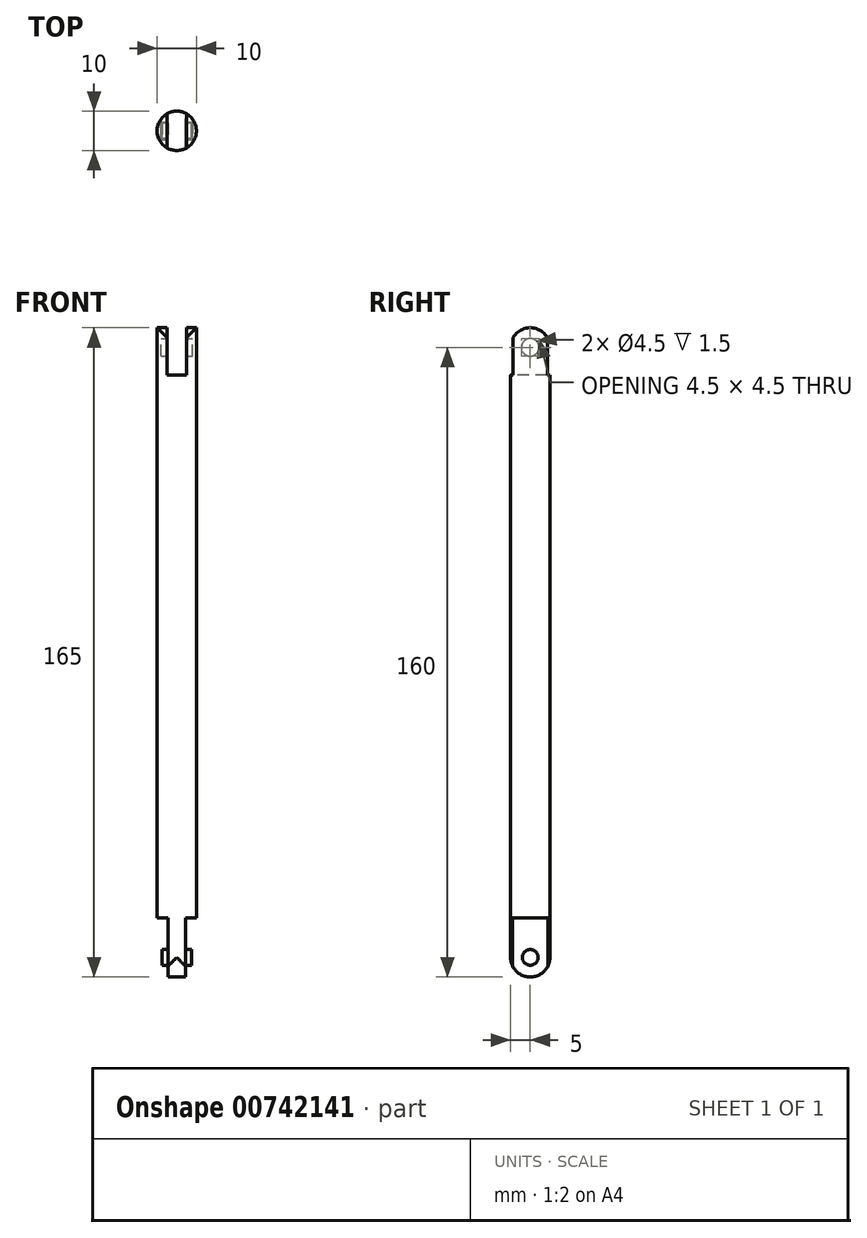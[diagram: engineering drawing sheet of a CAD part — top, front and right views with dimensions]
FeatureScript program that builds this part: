
annotation { "Feature Type Name" : "Feature", "Feature Type Description" : "" }
export const myFeature = defineFeature(function(context is Context, id is Id, definition is map)
    precondition{}
    {
        {
            var Q0;
            Q0=qCreatedBy(makeId("Top.planeOp"),FACE);
            var sketch = newSketch(context, id + "F0", { "sketchPlane" : qUnion([Q0])});
            skCircle(sketch, "E0", {"center": v(0, 0) * mm, "radius": 5 * mm});
            skSolve(sketch);
        }
        {
            var Q0;
            Q0=qSketchRegion(id+"F0",true);
            extrude(context, id + "F1", {"entities" : qUnion([Q0]), "depth" : 150 * mm, "offsetDistance" : 25 * mm});
        }
        {
            var Q0;
            Q0=makeQuery(id+"F1.opExtrude","CAP_FACE",FACE,{"disambiguationData":[OSD([sQuery(id+"F0.wireOp",EDGE,"E0")])],"isStart":true});
            var sketch = newSketch(context, id + "F2", { "sketchPlane" : qUnion([Q0])});
            skLineSegment(sketch, "E1.bottom", {"start": v(-2.2, 5) * mm, "end": v(2.2, 5) * mm});
            skLineSegment(sketch, "E1.top", {"start": v(-2.2, -5) * mm, "end": v(2.2, -5) * mm});
            skLineSegment(sketch, "E1.left", {"start": v(-2.2, 5) * mm, "end": v(-2.2, -5) * mm});
            skLineSegment(sketch, "E1.right", {"start": v(2.2, 5) * mm, "end": v(2.2, -5) * mm});
            skSolve(sketch);
        }
        {
            var Q0;
            {var subQ0=makeQuery(id+"F1.opExtrude","CAP_EDGE",EDGE,{"disambiguationData":[OSD([sQuery(id+"F0.wireOp",EDGE,"E0")])],"isStart":true});var subQ2=sQuery(id+"F2.wireOp",EDGE,"E1.left");var subQ3=makeQuery(id+"F2.imprint","INTERSECT",VERTEX,{"disambiguationData":[OD(0.0)],"derivedFrom":[subQ0,subQ2]});Q0=makeQuery(id+"F2.imprint","IMPRINT",FACE,{"disambiguationData":[TD([[makeQuery(id+"F2.imprint","IMPRINT",EDGE,{"disambiguationData":[TD([[subQ3,-1.0]])],"derivedFrom":subQ2}),1.0]])]});}
            extrude(context, id + "F3", {"entities" : qUnion([Q0]), "operationType" : NewBodyOperationType.ADD, "depth" : 15 * mm, "offsetDistance" : 25 * mm});
        }
        {
            var Q0;
            Q0=makeQuery(id+"F3.opExtrude","SWEPT_FACE",FACE,{"disambiguationData":[OSD([sQuery(id+"F2.wireOp",EDGE,"E1.right")])]});
            var sketch = newSketch(context, id + "F4", { "sketchPlane" : qUnion([Q0])});
            skCircle(sketch, "E2", {"center": v(0, -10) * mm, "radius": 5 * mm});
            skLineSegment(sketch, "E3", {"start": v(0, -10) * mm, "end": v(0, -15) * mm, "construction": true});
            skLineSegment(sketch, "E4", {"start": v(5, -10) * mm, "end": v(5, -15) * mm});
            skLineSegment(sketch, "E5", {"start": v(5, -15) * mm, "end": v(-5, -15) * mm});
            skLineSegment(sketch, "E6", {"start": v(-5, -15) * mm, "end": v(-5, -10) * mm});
            skSolve(sketch);
        }
        {
            var Q0;
            {var subQ0=sQuery(id+"F4.wireOp",EDGE,"E4");Q0=makeQuery(id+"F4.imprint","IMPRINT",FACE,{"disambiguationData":[TD([[makeQuery(id+"F4.imprint","IMPRINT",EDGE,{"derivedFrom":subQ0}),-1.0]])]});}
            var Q1;
            {var subQ0=sQuery(id+"F4.wireOp",EDGE,"E5");var subQ1=sQuery(id+"F4.wireOp",EDGE,"E2");var subQ2=makeQuery(id+"F4.imprint","INTERSECT",VERTEX,{"derivedFrom":[subQ1,subQ0]});Q1=makeQuery(id+"F4.imprint","IMPRINT",FACE,{"disambiguationData":[TD([[makeQuery(id+"F4.imprint","IMPRINT",EDGE,{"disambiguationData":[TD([[subQ2,-1.0]])],"derivedFrom":subQ1}),-1.0]])]});}
            var Q2;
            {var subQ0=sQuery(id+"F4.wireOp",EDGE,"E5");var subQ1=sQuery(id+"F4.wireOp",EDGE,"E2");var subQ2=makeQuery(id+"F4.imprint","INTERSECT",VERTEX,{"derivedFrom":[subQ1,subQ0]});Q2=makeQuery(id+"F4.imprint","IMPRINT",FACE,{"disambiguationData":[TD([[makeQuery(id+"F4.imprint","IMPRINT",EDGE,{"disambiguationData":[TD([[subQ2,1.0]])],"derivedFrom":subQ1}),-1.0]])]});}
            var Q3;
            {var subQ0=sQuery(id+"F4.wireOp",EDGE,"E6");Q3=makeQuery(id+"F4.imprint","IMPRINT",FACE,{"disambiguationData":[TD([[makeQuery(id+"F4.imprint","IMPRINT",EDGE,{"derivedFrom":subQ0}),-1.0]])]});}
            extrude(context, id + "F5", {"entities" : qUnion([Q0, Q1, Q2, Q3]), "operationType" : NewBodyOperationType.REMOVE, "oppositeDirection" : true, "depth" : 25 * mm, "offsetDistance" : 25 * mm});
        }
        {
            var Q0;
            Q0=makeQuery(id+"F3.opExtrude","SWEPT_FACE",FACE,{"disambiguationData":[OSD([sQuery(id+"F2.wireOp",EDGE,"E1.right")])]});
            var sketch = newSketch(context, id + "F6", { "sketchPlane" : qUnion([Q0])});
            skCircle(sketch, "E7", {"center": v(0, -10) * mm, "radius": 2 * mm});
            skSolve(sketch);
        }
        {
            var Q0;
            Q0=makeQuery(id+"F6.imprint","IMPRINT",FACE,{"disambiguationData":[TD([[makeQuery(id+"F6.imprint","IMPRINT",EDGE,{"derivedFrom":sQuery(id+"F6.wireOp",EDGE,"E7")}),1.0]])]});
            extrude(context, id + "F7", {"entities" : qUnion([Q0]), "operationType" : NewBodyOperationType.ADD, "depth" : 1.6 * mm, "offsetDistance" : 25 * mm, "hasSecondDirection" : true, "secondDirectionOppositeDirection" : true, "secondDirectionDepth" : 6 * mm});
        }
        {
            var Q0;
            Q0=makeQuery(id+"F1.opExtrude","CAP_FACE",FACE,{"disambiguationData":[OSD([sQuery(id+"F0.wireOp",EDGE,"E0")])],"isStart":false});
            var sketch = newSketch(context, id + "F8", { "sketchPlane" : qUnion([Q0])});
            skLineSegment(sketch, "E8.bottom", {"start": v(-2.5, 5) * mm, "end": v(2.5, 5) * mm});
            skLineSegment(sketch, "E8.top", {"start": v(-2.5, -5) * mm, "end": v(2.5, -5) * mm});
            skLineSegment(sketch, "E8.left", {"start": v(-2.5, 5) * mm, "end": v(-2.5, -5) * mm});
            skLineSegment(sketch, "E8.right", {"start": v(2.5, 5) * mm, "end": v(2.5, -5) * mm});
            skCircle(sketch, "E9.0", {"center": v(0, 0) * mm, "radius": 5 * mm});
            skSolve(sketch);
        }
        {
            var Q0;
            {var subQ0=sQuery(id+"F8.wireOp",EDGE,"E9.0");var subQ2=sQuery(id+"F8.wireOp",EDGE,"E8.left");var subQ3=makeQuery(id+"F8.imprint","INTERSECT",VERTEX,{"disambiguationData":[OD(0.0)],"derivedFrom":[subQ2,subQ0]});Q0=makeQuery(id+"F8.imprint","IMPRINT",FACE,{"disambiguationData":[TD([[makeQuery(id+"F8.imprint","IMPRINT",EDGE,{"disambiguationData":[TD([[subQ3,-1.0]])],"derivedFrom":subQ2}),1.0]])]});}
            extrude(context, id + "F9", {"entities" : qUnion([Q0]), "operationType" : NewBodyOperationType.REMOVE, "oppositeDirection" : true, "depth" : 12 * mm, "offsetDistance" : 25 * mm});
        }
        {
            var Q0;
            Q0=makeQuery(id+"F9.boolean.opBoolean","COPY",FACE,{"derivedFrom":makeQuery(id+"F9.opExtrude","SWEPT_FACE",FACE,{"disambiguationData":[OSD([sQuery(id+"F8.wireOp",EDGE,"E8.left")])]})});
            var sketch = newSketch(context, id + "F10", { "sketchPlane" : qUnion([Q0])});
            skCircle(sketch, "E10", {"center": v(0, 145) * mm, "radius": 2.25 * mm});
            skLineSegment(sketch, "E11", {"start": v(0, 145) * mm, "end": v(0, 150) * mm, "construction": true});
            skSolve(sketch);
        }
        {
            var Q0;
            Q0=makeQuery(id+"F10.imprint","IMPRINT",FACE,{"disambiguationData":[TD([[makeQuery(id+"F10.imprint","IMPRINT",EDGE,{"derivedFrom":sQuery(id+"F10.wireOp",EDGE,"E10")}),1.0]])]});
            extrude(context, id + "F11", {"entities" : qUnion([Q0]), "operationType" : NewBodyOperationType.REMOVE, "oppositeDirection" : true, "depth" : 1.5 * mm, "offsetDistance" : 25 * mm, "hasSecondDirection" : true, "secondDirectionOppositeDirection" : false, "secondDirectionDepth" : 6.5 * mm});
        }
        {
            var Q0;
            Q0=makeQuery(id+"F9.boolean.opBoolean","COPY",FACE,{"derivedFrom":makeQuery(id+"F9.opExtrude","SWEPT_FACE",FACE,{"disambiguationData":[OSD([sQuery(id+"F8.wireOp",EDGE,"E8.left")])]})});
            var sketch = newSketch(context, id + "F12", { "sketchPlane" : qUnion([Q0])});
            skCircle(sketch, "E12", {"center": v(0, 145) * mm, "radius": 5 * mm});
            skSolve(sketch);
        }
        {
            var Q0;
            {var subQ0=sQuery(id+"F12.wireOp",EDGE,"E12");var subQ1=sQuery(id+"F8.wireOp",EDGE,"E8.left");var subQ2=makeQuery(id+"F9.boolean.opBoolean","COPY",EDGE,{"derivedFrom":makeQuery(id+"F9.opExtrude","CAP_EDGE",EDGE,{"disambiguationData":[OSD([subQ1])],"isStart":true})});var subQ3=makeQuery(id+"F12.imprint","INTERSECT",VERTEX,{"derivedFrom":[subQ2,subQ0]});Q0=makeQuery(id+"F12.imprint","IMPRINT",FACE,{"disambiguationData":[TD([[makeQuery(id+"F12.imprint","IMPRINT",EDGE,{"disambiguationData":[TD([[subQ3,1.0]])],"derivedFrom":subQ0}),-1.0]])]});}
            var Q1;
            {var subQ0=sQuery(id+"F12.wireOp",EDGE,"E12");var subQ1=sQuery(id+"F8.wireOp",EDGE,"E8.left");var subQ2=makeQuery(id+"F9.boolean.opBoolean","COPY",EDGE,{"derivedFrom":makeQuery(id+"F9.opExtrude","CAP_EDGE",EDGE,{"disambiguationData":[OSD([subQ1])],"isStart":true})});var subQ3=makeQuery(id+"F12.imprint","INTERSECT",VERTEX,{"derivedFrom":[subQ2,subQ0]});Q1=makeQuery(id+"F12.imprint","IMPRINT",FACE,{"disambiguationData":[TD([[makeQuery(id+"F12.imprint","IMPRINT",EDGE,{"disambiguationData":[TD([[subQ3,-1.0]])],"derivedFrom":subQ0}),-1.0]])]});}
            extrude(context, id + "F13", {"entities" : qUnion([Q0, Q1]), "operationType" : NewBodyOperationType.REMOVE, "endBound" : BoundingType.THROUGH_ALL, "oppositeDirection" : true, "depth" : 25 * mm, "offsetDistance" : 25 * mm, "hasSecondDirection" : true, "secondDirectionBound" : SecondDirectionBoundingType.THROUGH_ALL, "secondDirectionOppositeDirection" : false, "secondDirectionDepth" : 25 * mm});
        }
    });
